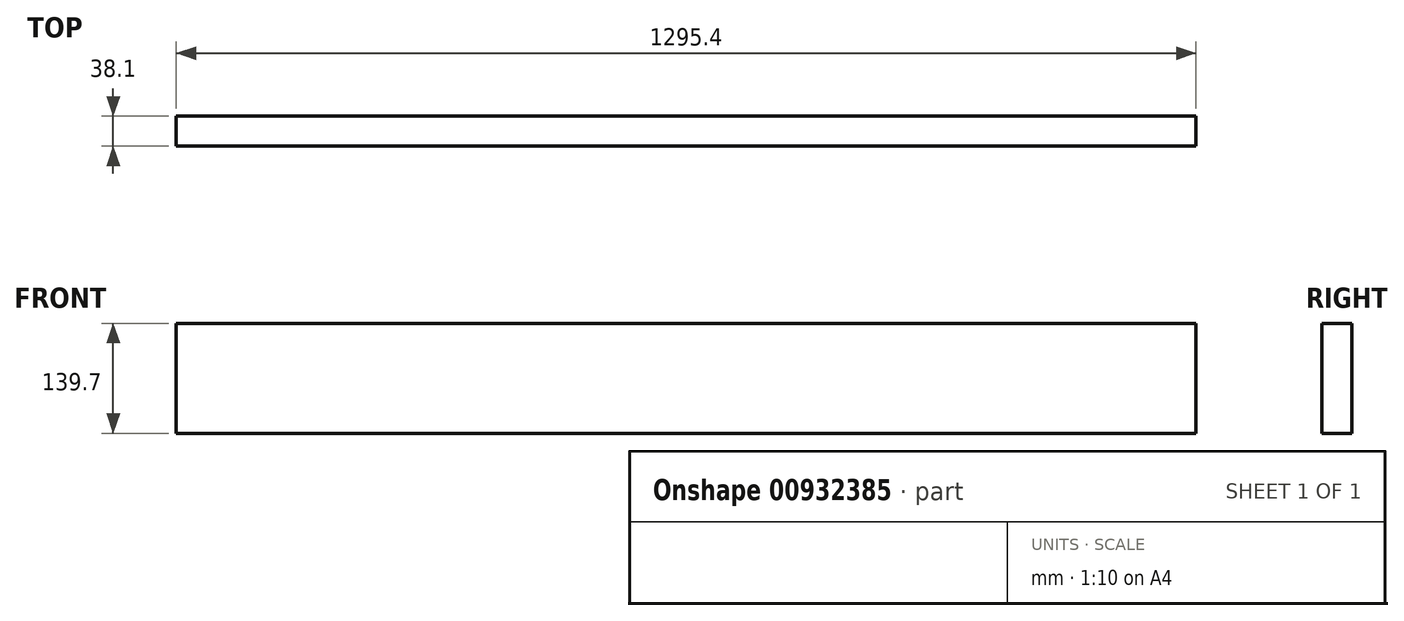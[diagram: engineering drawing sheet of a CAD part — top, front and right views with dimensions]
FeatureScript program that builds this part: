
annotation { "Feature Type Name" : "Feature", "Feature Type Description" : "" }
export const myFeature = defineFeature(function(context is Context, id is Id, definition is map)
    precondition{}
    {
        {
            var Q0;
            Q0=qCreatedBy(makeId("Right.planeOp"),FACE);
            var sketch = newSketch(context, id + "F0", { "sketchPlane" : qUnion([Q0])});
            skLineSegment(sketch, "E0.bottom", {"start": v(19.05, 69.85) * mm, "end": v(-19.05, 69.85) * mm});
            skLineSegment(sketch, "E0.top", {"start": v(19.05, -69.85) * mm, "end": v(-19.05, -69.85) * mm});
            skLineSegment(sketch, "E0.left", {"start": v(19.05, 69.85) * mm, "end": v(19.05, -69.85) * mm});
            skLineSegment(sketch, "E0.right", {"start": v(-19.05, 69.85) * mm, "end": v(-19.05, -69.85) * mm});
            skPoint(sketch, "E0.middle", {"position": v(0, 0) * mm});
            skSolve(sketch);
        }
        {
            var Q0;
            Q0=makeQuery(id+"F0.imprint","IMPRINT",FACE,{"disambiguationData":[TD([[makeQuery(id+"F0.imprint","IMPRINT",EDGE,{"derivedFrom":sQuery(id+"F0.wireOp",EDGE,"E0.bottom")}),1.0]])]});
            extrude(context, id + "F1", {"entities" : qUnion([Q0]), "depth" : 1295.4 * mm, "offsetDistance" : 25.4 * mm});
        }
    });
